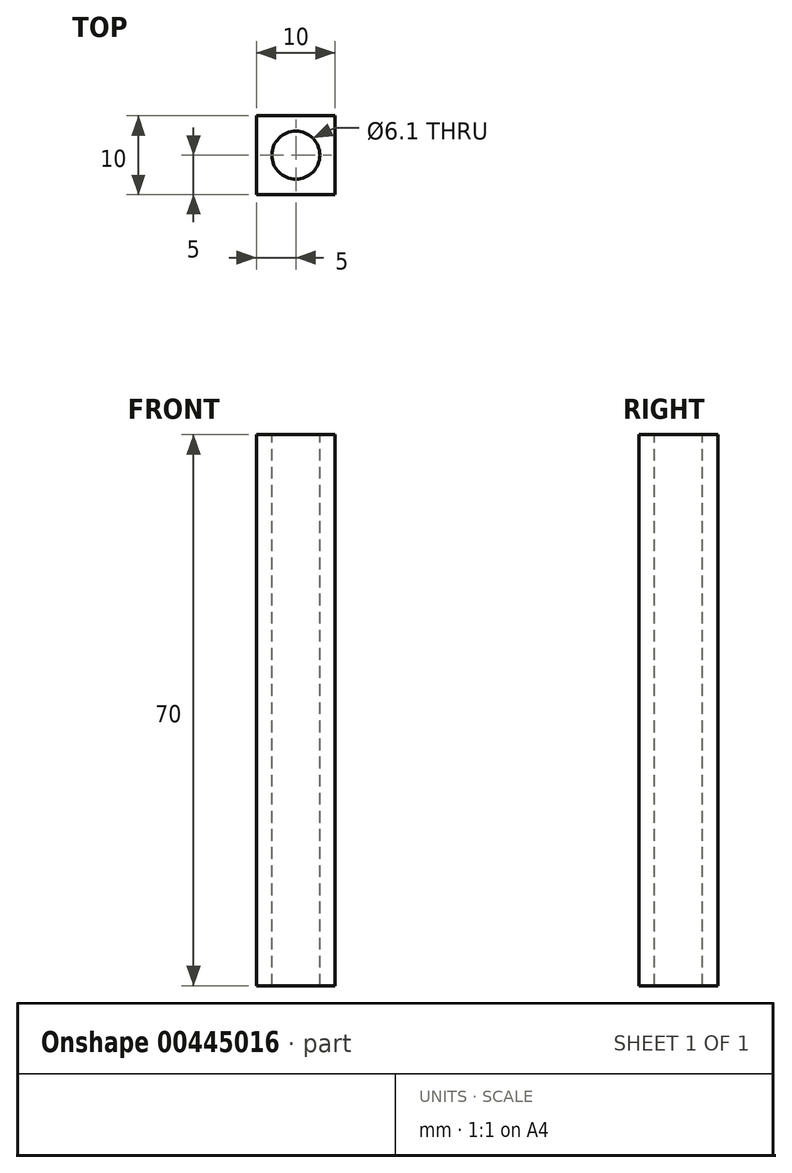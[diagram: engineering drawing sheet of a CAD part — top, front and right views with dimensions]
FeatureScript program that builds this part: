
annotation { "Feature Type Name" : "Feature", "Feature Type Description" : "" }
export const myFeature = defineFeature(function(context is Context, id is Id, definition is map)
    precondition{}
    {
        {
            var Q0;
            Q0=qCreatedBy(makeId("Top.planeOp"),FACE);
            var sketch = newSketch(context, id + "F0", { "sketchPlane" : qUnion([Q0])});
            skLineSegment(sketch, "E0.bottom", {"start": v(5, 5) * mm, "end": v(-5, 5) * mm});
            skLineSegment(sketch, "E0.top", {"start": v(5, -5) * mm, "end": v(-5, -5) * mm});
            skLineSegment(sketch, "E0.left", {"start": v(5, 5) * mm, "end": v(5, -5) * mm});
            skLineSegment(sketch, "E0.right", {"start": v(-5, 5) * mm, "end": v(-5, -5) * mm});
            skPoint(sketch, "E0.middle", {"position": v(0, 0) * mm});
            skSolve(sketch);
        }
        {
            var Q0;
            Q0=makeQuery(id+"F0.imprint","IMPRINT",FACE,{"disambiguationData":[TD([[makeQuery(id+"F0.imprint","IMPRINT",EDGE,{"derivedFrom":sQuery(id+"F0.wireOp",EDGE,"E0.bottom")}),1.0]])]});
            extrude(context, id + "F1", {"entities" : qUnion([Q0]), "depth" : 70 * mm, "offsetDistance" : 25 * mm});
        }
        {
            var Q0;
            Q0=makeQuery(id+"F1.opExtrude","CAP_FACE",FACE,{"disambiguationData":[OSD([sQuery(id+"F0.wireOp",EDGE,"E0.bottom"),sQuery(id+"F0.wireOp",EDGE,"E0.top"),sQuery(id+"F0.wireOp",EDGE,"E0.left"),sQuery(id+"F0.wireOp",EDGE,"E0.right")])],"isStart":false});
            var sketch = newSketch(context, id + "F2", { "sketchPlane" : qUnion([Q0])});
            skPoint(sketch, "E1", {"position": v(0, 0) * mm});
            skSolve(sketch);
        }
        {
            var Q0;
            Q0=sQuery(id+"F2.wireOp",VERTEX,"E1");
            var Q1;
            Q1=makeQuery(id+"F1.opExtrude","SWEPT_BODY",BODY,{"disambiguationData":[OSD([sQuery(id+"F0.wireOp",EDGE,"E0.bottom"),sQuery(id+"F0.wireOp",EDGE,"E0.top"),sQuery(id+"F0.wireOp",EDGE,"E0.left"),sQuery(id+"F0.wireOp",EDGE,"E0.right")])]});
            hole(context, id + "F3", {"style" : HoleStyle.SIMPLE, "endStyle" : HoleEndStyle.BLIND, "holeDiameter" : 6.1 * mm, "majorDiameter" : 5 * mm, "holeDepth" : 1000 * mm, "isTappedThrough" : true, "tappedDepth" : 12 * mm, "tapClearance" : 3, "locations" : qUnion([Q0]), "scope" : qUnion([Q1])});
        }
    });
